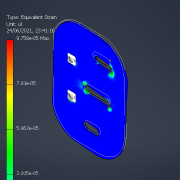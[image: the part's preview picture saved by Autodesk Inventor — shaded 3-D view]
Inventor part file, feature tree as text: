
AUTODESK INVENTOR PART (.ipt)
format: ipt  version: 2021 (Build 250183000, 183)  size: 509,952 bytes
history: native  units: mm
features: sketch x3, extrude x2, hole x2, fillet x1
ambient origin geometry x8: Origin, YZ Plane, XZ Plane, XY Plane, X Axis, Y Axis, Z Axis, Center Point
bodies: Solid1 (feature_tree)
feature tree (8):
  sketch  "Sketch1"  dims[d4=2190.0mm d5=3.0mm d6=0.0mm]
  extrude  "Extrusion1"  Depth=3.0mm TaperAngle=0.0deg
  hole  "Hole1"  [1 undecoded]
  extrude  "Extrusion2"  Depth=40.0mm
  hole  "Hole2"  [1 undecoded]
  fillet  "Fillet1"  Radius=30.0mm
  sketch  "Sketch2"  dims[d10=50.0mm d11=50.0mm]
  sketch  "Sketch3"  dims[d12=12.0mm d13=6.0mm d14=4.0mm d15=2.0mm d16=90.0deg d17=8.0mm d18=20.594885mm d21=305.2mm d23=3.0mm d24=0.0mm d29=8.0mm d30=6.0mm d31=4.0mm d32=2.0mm d33=90.0deg d34=8.0mm d35=20.594885mm d36=30.0mm d37=30.0mm d38=27.5mm d39=55.0mm d40=27.5mm d41=27.5mm d44=38.0mm d45=38.0mm d46=19.0mm d47=19.0mm d48=40.0mm]
note: 2 required parameter values undecoded (feature->parameter linkage not recoverable at this tier; creation-order binding heuristic only, values carry confidence <= 0.55)
